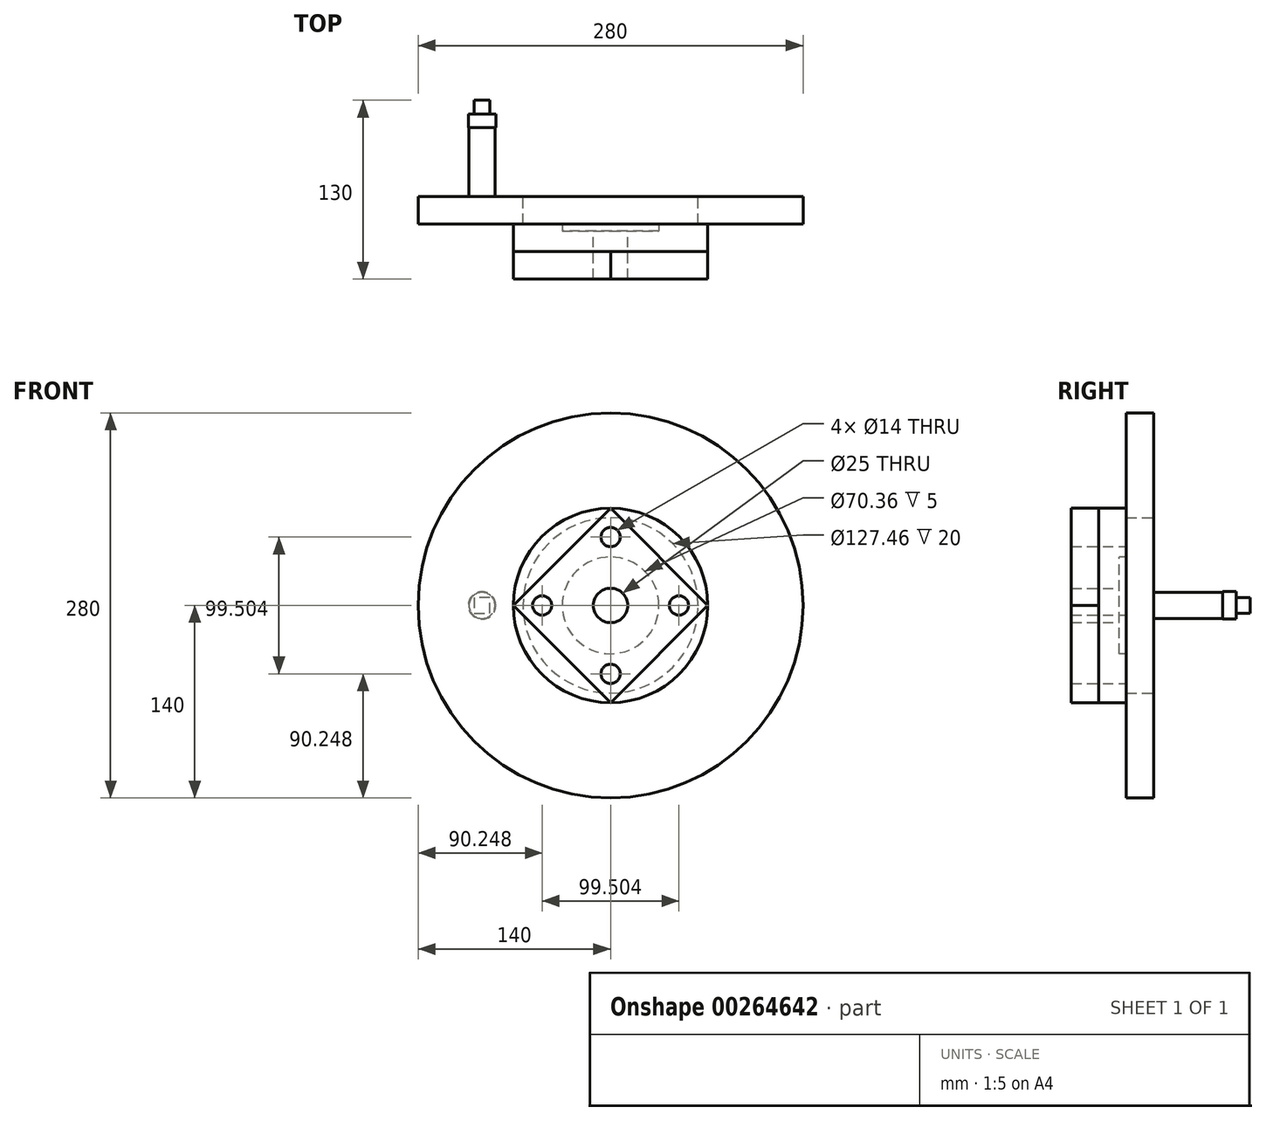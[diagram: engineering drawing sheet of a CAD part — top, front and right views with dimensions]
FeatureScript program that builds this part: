
annotation { "Feature Type Name" : "Feature", "Feature Type Description" : "" }
export const myFeature = defineFeature(function(context is Context, id is Id, definition is map)
    precondition{}
    {
        {
            var Q0;
            Q0=qCreatedBy(makeId("Front.planeOp"),FACE);
            var sketch = newSketch(context, id + "F0", { "sketchPlane" : qUnion([Q0])});
            skLineSegment(sketch, "E0", {"start": v(70.71, 0) * mm, "end": v(0, 70.71) * mm});
            skLineSegment(sketch, "E1", {"start": v(0, 70.71) * mm, "end": v(-70.71, 0) * mm});
            skLineSegment(sketch, "E2", {"start": v(-70.71, 0) * mm, "end": v(0, -70.71) * mm});
            skLineSegment(sketch, "E3", {"start": v(0, -70.71) * mm, "end": v(70.71, 0) * mm});
            skLineSegment(sketch, "E4", {"start": v(0, -49.75) * mm, "end": v(-49.75, 0) * mm, "construction": true});
            skLineSegment(sketch, "E5", {"start": v(-49.75, 0) * mm, "end": v(0, 49.75) * mm, "construction": true});
            skLineSegment(sketch, "E6", {"start": v(0, 49.75) * mm, "end": v(49.75, 0) * mm, "construction": true});
            skLineSegment(sketch, "E7", {"start": v(49.75, 0) * mm, "end": v(0, -49.75) * mm, "construction": true});
            skCircle(sketch, "E8", {"center": v(49.75, 0) * mm, "radius": 7 * mm});
            skCircle(sketch, "E9", {"center": v(0, 49.75) * mm, "radius": 7 * mm});
            skCircle(sketch, "E10", {"center": v(-49.75, 0) * mm, "radius": 7 * mm});
            skCircle(sketch, "E11", {"center": v(0, -49.75) * mm, "radius": 7 * mm});
            skCircle(sketch, "E12", {"center": v(0, 0) * mm, "radius": 35.18 * mm});
            skCircle(sketch, "E13", {"center": v(0, 0) * mm, "radius": 42.75 * mm});
            skCircle(sketch, "E14", {"center": v(0, 0) * mm, "radius": 70.71 * mm});
            skCircle(sketch, "E15", {"center": v(0, 0) * mm, "radius": 12.5 * mm});
            skCircle(sketch, "E16", {"center": v(-93.5, 0) * mm, "radius": 9.5 * mm});
            skCircle(sketch, "E17", {"center": v(0, 0) * mm, "radius": 56.75 * mm});
            skCircle(sketch, "E18", {"center": v(0, 0) * mm, "radius": 63.73 * mm});
            skLineSegment(sketch, "E19", {"start": v(0, 70.71) * mm, "end": v(0, 63.73) * mm, "construction": true});
            skLineSegment(sketch, "E20", {"start": v(0, 63.73) * mm, "end": v(0, 56.75) * mm, "construction": true});
            skCircle(sketch, "E21", {"center": v(0, 0) * mm, "radius": 140 * mm});
            skSolve(sketch);
        }
        {
            var Q0;
            {var subQ1=sQuery(id+"F0.wireOp",EDGE,"E0");var subQ3=sQuery(id+"F0.wireOp",EDGE,"E18");var subQ4=makeQuery(id+"F0.imprint","INTERSECT",VERTEX,{"disambiguationData":[OD(0.0)],"derivedFrom":[subQ1,subQ3]});Q0=makeQuery(id+"F0.imprint","IMPRINT",FACE,{"disambiguationData":[TD([[makeQuery(id+"F0.imprint","IMPRINT",EDGE,{"disambiguationData":[TD([[subQ4,1.0]])],"derivedFrom":subQ3}),-1.0]])]});}
            var Q1;
            {var subQ4=sQuery(id+"F0.wireOp",EDGE,"E0");var subQ6=sQuery(id+"F0.wireOp",EDGE,"E18");var subQ8=makeQuery(id+"F0.imprint","INTERSECT",VERTEX,{"disambiguationData":[OD(0.0)],"derivedFrom":[subQ4,subQ6]});Q1=makeQuery(id+"F0.imprint","IMPRINT",FACE,{"disambiguationData":[TD([[makeQuery(id+"F0.imprint","IMPRINT",EDGE,{"disambiguationData":[TD([[subQ8,-1.0]])],"derivedFrom":subQ4}),1.0]])]});}
            var Q2;
            {var subQ5=sQuery(id+"F0.wireOp",EDGE,"E17");var subQ8=sQuery(id+"F0.wireOp",EDGE,"E0");var subQ9=makeQuery(id+"F0.imprint","INTERSECT",VERTEX,{"disambiguationData":[OD(0.0)],"derivedFrom":[subQ8,subQ5]});Q2=makeQuery(id+"F0.imprint","IMPRINT",FACE,{"disambiguationData":[TD([[makeQuery(id+"F0.imprint","IMPRINT",EDGE,{"disambiguationData":[TD([[subQ9,-1.0]])],"derivedFrom":subQ8}),1.0]])]});}
            var Q3;
            {var subQ0=sQuery(id+"F0.wireOp",EDGE,"E17");var subQ4=sQuery(id+"F0.wireOp",EDGE,"E0");var subQ5=makeQuery(id+"F0.imprint","INTERSECT",VERTEX,{"disambiguationData":[OD(1.0)],"derivedFrom":[subQ4,subQ0]});Q3=makeQuery(id+"F0.imprint","IMPRINT",FACE,{"disambiguationData":[TD([[makeQuery(id+"F0.imprint","IMPRINT",EDGE,{"disambiguationData":[TD([[subQ5,-1.0]])],"derivedFrom":subQ4}),1.0]])]});}
            var Q4;
            {var subQ1=sQuery(id+"F0.wireOp",EDGE,"E0");var subQ3=sQuery(id+"F0.wireOp",EDGE,"E18");var subQ4=makeQuery(id+"F0.imprint","INTERSECT",VERTEX,{"disambiguationData":[OD(1.0)],"derivedFrom":[subQ1,subQ3]});Q4=makeQuery(id+"F0.imprint","IMPRINT",FACE,{"disambiguationData":[TD([[makeQuery(id+"F0.imprint","IMPRINT",EDGE,{"disambiguationData":[TD([[subQ4,-1.0]])],"derivedFrom":subQ3}),-1.0]])]});}
            var Q5;
            {var subQ5=sQuery(id+"F0.wireOp",EDGE,"E17");var subQ8=sQuery(id+"F0.wireOp",EDGE,"E1");var subQ10=makeQuery(id+"F0.imprint","INTERSECT",VERTEX,{"disambiguationData":[OD(0.0)],"derivedFrom":[subQ8,subQ5]});Q5=makeQuery(id+"F0.imprint","IMPRINT",FACE,{"disambiguationData":[TD([[makeQuery(id+"F0.imprint","IMPRINT",EDGE,{"disambiguationData":[TD([[subQ10,-1.0]])],"derivedFrom":subQ8}),1.0]])]});}
            var Q6;
            Q6=makeQuery(id+"F0.imprint","IMPRINT",FACE,{"disambiguationData":[TD([[makeQuery(id+"F0.imprint","IMPRINT",EDGE,{"derivedFrom":sQuery(id+"F0.wireOp",EDGE,"E12")}),-1.0]])]});
            var Q7;
            {var subQ3=sQuery(id+"F0.wireOp",EDGE,"E17");var subQ8=sQuery(id+"F0.wireOp",EDGE,"E3");var subQ9=makeQuery(id+"F0.imprint","INTERSECT",VERTEX,{"disambiguationData":[OD(0.0)],"derivedFrom":[subQ8,subQ3]});Q7=makeQuery(id+"F0.imprint","IMPRINT",FACE,{"disambiguationData":[TD([[makeQuery(id+"F0.imprint","IMPRINT",EDGE,{"disambiguationData":[TD([[subQ9,-1.0]])],"derivedFrom":subQ8}),1.0]])]});}
            var Q8;
            {var subQ5=sQuery(id+"F0.wireOp",EDGE,"E17");var subQ8=sQuery(id+"F0.wireOp",EDGE,"E2");var subQ10=makeQuery(id+"F0.imprint","INTERSECT",VERTEX,{"disambiguationData":[OD(0.0)],"derivedFrom":[subQ8,subQ5]});Q8=makeQuery(id+"F0.imprint","IMPRINT",FACE,{"disambiguationData":[TD([[makeQuery(id+"F0.imprint","IMPRINT",EDGE,{"disambiguationData":[TD([[subQ10,-1.0]])],"derivedFrom":subQ8}),1.0]])]});}
            var Q9;
            {var subQ0=sQuery(id+"F0.wireOp",EDGE,"E17");var subQ1=sQuery(id+"F0.wireOp",EDGE,"E2");var subQ2=makeQuery(id+"F0.imprint","INTERSECT",VERTEX,{"disambiguationData":[OD(1.0)],"derivedFrom":[subQ1,subQ0]});Q9=makeQuery(id+"F0.imprint","IMPRINT",FACE,{"disambiguationData":[TD([[makeQuery(id+"F0.imprint","IMPRINT",EDGE,{"disambiguationData":[TD([[subQ2,-1.0]])],"derivedFrom":subQ1}),1.0]])]});}
            var Q10;
            {var subQ1=sQuery(id+"F0.wireOp",EDGE,"E2");var subQ3=sQuery(id+"F0.wireOp",EDGE,"E18");var subQ4=makeQuery(id+"F0.imprint","INTERSECT",VERTEX,{"disambiguationData":[OD(1.0)],"derivedFrom":[subQ1,subQ3]});Q10=makeQuery(id+"F0.imprint","IMPRINT",FACE,{"disambiguationData":[TD([[makeQuery(id+"F0.imprint","IMPRINT",EDGE,{"disambiguationData":[TD([[subQ4,-1.0]])],"derivedFrom":subQ3}),-1.0]])]});}
            var Q11;
            {var subQ0=sQuery(id+"F0.wireOp",EDGE,"E17");var subQ4=sQuery(id+"F0.wireOp",EDGE,"E1");var subQ5=makeQuery(id+"F0.imprint","INTERSECT",VERTEX,{"disambiguationData":[OD(1.0)],"derivedFrom":[subQ4,subQ0]});Q11=makeQuery(id+"F0.imprint","IMPRINT",FACE,{"disambiguationData":[TD([[makeQuery(id+"F0.imprint","IMPRINT",EDGE,{"disambiguationData":[TD([[subQ5,-1.0]])],"derivedFrom":subQ4}),1.0]])]});}
            var Q12;
            {var subQ1=sQuery(id+"F0.wireOp",EDGE,"E1");var subQ3=sQuery(id+"F0.wireOp",EDGE,"E18");var subQ4=makeQuery(id+"F0.imprint","INTERSECT",VERTEX,{"disambiguationData":[OD(1.0)],"derivedFrom":[subQ1,subQ3]});Q12=makeQuery(id+"F0.imprint","IMPRINT",FACE,{"disambiguationData":[TD([[makeQuery(id+"F0.imprint","IMPRINT",EDGE,{"disambiguationData":[TD([[subQ4,-1.0]])],"derivedFrom":subQ3}),-1.0]])]});}
            var Q13;
            Q13=makeQuery(id+"F0.imprint","IMPRINT",FACE,{"disambiguationData":[TD([[makeQuery(id+"F0.imprint","IMPRINT",EDGE,{"derivedFrom":sQuery(id+"F0.wireOp",EDGE,"E12")}),1.0]])]});
            extrude(context, id + "F1", {"entities" : qUnion([Q0, Q1, Q2, Q3, Q4, Q5, Q6, Q7, Q8, Q9, Q10, Q11, Q12, Q13]), "depth" : 20 * mm});
        }
        {
            var Q0;
            Q0=makeQuery(id+"F0.imprint","IMPRINT",FACE,{"disambiguationData":[TD([[makeQuery(id+"F0.imprint","IMPRINT",EDGE,{"derivedFrom":sQuery(id+"F0.wireOp",EDGE,"E12")}),1.0]])]});
            extrude(context, id + "F2", {"entities" : qUnion([Q0]), "operationType" : NewBodyOperationType.ADD, "oppositeDirection" : true, "depth" : 15 * mm});
        }
        {
            var Q0;
            Q0=makeQuery(id+"F0.imprint","IMPRINT",FACE,{"disambiguationData":[TD([[makeQuery(id+"F0.imprint","IMPRINT",EDGE,{"derivedFrom":sQuery(id+"F0.wireOp",EDGE,"E12")}),-1.0]])]});
            var Q1;
            {var subQ3=sQuery(id+"F0.wireOp",EDGE,"E17");var subQ8=sQuery(id+"F0.wireOp",EDGE,"E3");var subQ9=makeQuery(id+"F0.imprint","INTERSECT",VERTEX,{"disambiguationData":[OD(0.0)],"derivedFrom":[subQ8,subQ3]});Q1=makeQuery(id+"F0.imprint","IMPRINT",FACE,{"disambiguationData":[TD([[makeQuery(id+"F0.imprint","IMPRINT",EDGE,{"disambiguationData":[TD([[subQ9,-1.0]])],"derivedFrom":subQ8}),1.0]])]});}
            var Q2;
            {var subQ0=sQuery(id+"F0.wireOp",EDGE,"E17");var subQ1=sQuery(id+"F0.wireOp",EDGE,"E3");var subQ2=makeQuery(id+"F0.imprint","INTERSECT",VERTEX,{"disambiguationData":[OD(0.0)],"derivedFrom":[subQ1,subQ0]});Q2=makeQuery(id+"F0.imprint","IMPRINT",FACE,{"disambiguationData":[TD([[makeQuery(id+"F0.imprint","IMPRINT",EDGE,{"disambiguationData":[TD([[subQ2,-1.0]])],"derivedFrom":subQ1}),-1.0]])]});}
            var Q3;
            {var subQ0=sQuery(id+"F0.wireOp",EDGE,"E18");var subQ1=sQuery(id+"F0.wireOp",EDGE,"E3");var subQ2=makeQuery(id+"F0.imprint","INTERSECT",VERTEX,{"disambiguationData":[OD(0.0)],"derivedFrom":[subQ1,subQ0]});Q3=makeQuery(id+"F0.imprint","IMPRINT",FACE,{"disambiguationData":[TD([[makeQuery(id+"F0.imprint","IMPRINT",EDGE,{"disambiguationData":[TD([[subQ2,-1.0]])],"derivedFrom":subQ1}),-1.0]])]});}
            var Q4;
            {var subQ1=sQuery(id+"F0.wireOp",EDGE,"E3");var subQ3=sQuery(id+"F0.wireOp",EDGE,"E18");var subQ4=makeQuery(id+"F0.imprint","INTERSECT",VERTEX,{"disambiguationData":[OD(0.0)],"derivedFrom":[subQ1,subQ3]});Q4=makeQuery(id+"F0.imprint","IMPRINT",FACE,{"disambiguationData":[TD([[makeQuery(id+"F0.imprint","IMPRINT",EDGE,{"disambiguationData":[TD([[subQ4,-1.0]])],"derivedFrom":subQ3}),-1.0]])]});}
            var Q5;
            {var subQ4=sQuery(id+"F0.wireOp",EDGE,"E0");var subQ6=sQuery(id+"F0.wireOp",EDGE,"E18");var subQ8=makeQuery(id+"F0.imprint","INTERSECT",VERTEX,{"disambiguationData":[OD(0.0)],"derivedFrom":[subQ4,subQ6]});Q5=makeQuery(id+"F0.imprint","IMPRINT",FACE,{"disambiguationData":[TD([[makeQuery(id+"F0.imprint","IMPRINT",EDGE,{"disambiguationData":[TD([[subQ8,-1.0]])],"derivedFrom":subQ4}),1.0]])]});}
            var Q6;
            {var subQ1=sQuery(id+"F0.wireOp",EDGE,"E0");var subQ3=sQuery(id+"F0.wireOp",EDGE,"E18");var subQ4=makeQuery(id+"F0.imprint","INTERSECT",VERTEX,{"disambiguationData":[OD(0.0)],"derivedFrom":[subQ1,subQ3]});Q6=makeQuery(id+"F0.imprint","IMPRINT",FACE,{"disambiguationData":[TD([[makeQuery(id+"F0.imprint","IMPRINT",EDGE,{"disambiguationData":[TD([[subQ4,1.0]])],"derivedFrom":subQ3}),-1.0]])]});}
            var Q7;
            {var subQ1=sQuery(id+"F0.wireOp",EDGE,"E0");var subQ3=sQuery(id+"F0.wireOp",EDGE,"E18");var subQ4=makeQuery(id+"F0.imprint","INTERSECT",VERTEX,{"disambiguationData":[OD(0.0)],"derivedFrom":[subQ1,subQ3]});Q7=makeQuery(id+"F0.imprint","IMPRINT",FACE,{"disambiguationData":[TD([[makeQuery(id+"F0.imprint","IMPRINT",EDGE,{"disambiguationData":[TD([[subQ4,-1.0]])],"derivedFrom":subQ3}),-1.0]])]});}
            var Q8;
            {var subQ0=sQuery(id+"F0.wireOp",EDGE,"E18");var subQ1=sQuery(id+"F0.wireOp",EDGE,"E0");var subQ2=makeQuery(id+"F0.imprint","INTERSECT",VERTEX,{"disambiguationData":[OD(0.0)],"derivedFrom":[subQ1,subQ0]});Q8=makeQuery(id+"F0.imprint","IMPRINT",FACE,{"disambiguationData":[TD([[makeQuery(id+"F0.imprint","IMPRINT",EDGE,{"disambiguationData":[TD([[subQ2,-1.0]])],"derivedFrom":subQ1}),-1.0]])]});}
            var Q9;
            {var subQ0=sQuery(id+"F0.wireOp",EDGE,"E17");var subQ1=sQuery(id+"F0.wireOp",EDGE,"E0");var subQ2=makeQuery(id+"F0.imprint","INTERSECT",VERTEX,{"disambiguationData":[OD(0.0)],"derivedFrom":[subQ1,subQ0]});Q9=makeQuery(id+"F0.imprint","IMPRINT",FACE,{"disambiguationData":[TD([[makeQuery(id+"F0.imprint","IMPRINT",EDGE,{"disambiguationData":[TD([[subQ2,-1.0]])],"derivedFrom":subQ1}),-1.0]])]});}
            var Q10;
            {var subQ5=sQuery(id+"F0.wireOp",EDGE,"E17");var subQ8=sQuery(id+"F0.wireOp",EDGE,"E0");var subQ9=makeQuery(id+"F0.imprint","INTERSECT",VERTEX,{"disambiguationData":[OD(0.0)],"derivedFrom":[subQ8,subQ5]});Q10=makeQuery(id+"F0.imprint","IMPRINT",FACE,{"disambiguationData":[TD([[makeQuery(id+"F0.imprint","IMPRINT",EDGE,{"disambiguationData":[TD([[subQ9,-1.0]])],"derivedFrom":subQ8}),1.0]])]});}
            var Q11;
            {var subQ0=sQuery(id+"F0.wireOp",EDGE,"E17");var subQ4=sQuery(id+"F0.wireOp",EDGE,"E0");var subQ5=makeQuery(id+"F0.imprint","INTERSECT",VERTEX,{"disambiguationData":[OD(1.0)],"derivedFrom":[subQ4,subQ0]});Q11=makeQuery(id+"F0.imprint","IMPRINT",FACE,{"disambiguationData":[TD([[makeQuery(id+"F0.imprint","IMPRINT",EDGE,{"disambiguationData":[TD([[subQ5,-1.0]])],"derivedFrom":subQ4}),1.0]])]});}
            var Q12;
            {var subQ1=sQuery(id+"F0.wireOp",EDGE,"E0");var subQ3=sQuery(id+"F0.wireOp",EDGE,"E18");var subQ4=makeQuery(id+"F0.imprint","INTERSECT",VERTEX,{"disambiguationData":[OD(1.0)],"derivedFrom":[subQ1,subQ3]});Q12=makeQuery(id+"F0.imprint","IMPRINT",FACE,{"disambiguationData":[TD([[makeQuery(id+"F0.imprint","IMPRINT",EDGE,{"disambiguationData":[TD([[subQ4,-1.0]])],"derivedFrom":subQ3}),-1.0]])]});}
            var Q13;
            {var subQ0=sQuery(id+"F0.wireOp",EDGE,"E18");var subQ1=sQuery(id+"F0.wireOp",EDGE,"E1");var subQ2=makeQuery(id+"F0.imprint","INTERSECT",VERTEX,{"disambiguationData":[OD(0.0)],"derivedFrom":[subQ1,subQ0]});Q13=makeQuery(id+"F0.imprint","IMPRINT",FACE,{"disambiguationData":[TD([[makeQuery(id+"F0.imprint","IMPRINT",EDGE,{"disambiguationData":[TD([[subQ2,-1.0]])],"derivedFrom":subQ1}),-1.0]])]});}
            var Q14;
            {var subQ0=sQuery(id+"F0.wireOp",EDGE,"E17");var subQ1=sQuery(id+"F0.wireOp",EDGE,"E1");var subQ2=makeQuery(id+"F0.imprint","INTERSECT",VERTEX,{"disambiguationData":[OD(0.0)],"derivedFrom":[subQ1,subQ0]});Q14=makeQuery(id+"F0.imprint","IMPRINT",FACE,{"disambiguationData":[TD([[makeQuery(id+"F0.imprint","IMPRINT",EDGE,{"disambiguationData":[TD([[subQ2,-1.0]])],"derivedFrom":subQ1}),-1.0]])]});}
            var Q15;
            {var subQ5=sQuery(id+"F0.wireOp",EDGE,"E17");var subQ8=sQuery(id+"F0.wireOp",EDGE,"E1");var subQ10=makeQuery(id+"F0.imprint","INTERSECT",VERTEX,{"disambiguationData":[OD(0.0)],"derivedFrom":[subQ8,subQ5]});Q15=makeQuery(id+"F0.imprint","IMPRINT",FACE,{"disambiguationData":[TD([[makeQuery(id+"F0.imprint","IMPRINT",EDGE,{"disambiguationData":[TD([[subQ10,-1.0]])],"derivedFrom":subQ8}),1.0]])]});}
            var Q16;
            {var subQ1=sQuery(id+"F0.wireOp",EDGE,"E1");var subQ3=sQuery(id+"F0.wireOp",EDGE,"E18");var subQ4=makeQuery(id+"F0.imprint","INTERSECT",VERTEX,{"disambiguationData":[OD(0.0)],"derivedFrom":[subQ1,subQ3]});Q16=makeQuery(id+"F0.imprint","IMPRINT",FACE,{"disambiguationData":[TD([[makeQuery(id+"F0.imprint","IMPRINT",EDGE,{"disambiguationData":[TD([[subQ4,-1.0]])],"derivedFrom":subQ3}),-1.0]])]});}
            var Q17;
            {var subQ0=sQuery(id+"F0.wireOp",EDGE,"E17");var subQ4=sQuery(id+"F0.wireOp",EDGE,"E1");var subQ5=makeQuery(id+"F0.imprint","INTERSECT",VERTEX,{"disambiguationData":[OD(1.0)],"derivedFrom":[subQ4,subQ0]});Q17=makeQuery(id+"F0.imprint","IMPRINT",FACE,{"disambiguationData":[TD([[makeQuery(id+"F0.imprint","IMPRINT",EDGE,{"disambiguationData":[TD([[subQ5,-1.0]])],"derivedFrom":subQ4}),1.0]])]});}
            var Q18;
            {var subQ1=sQuery(id+"F0.wireOp",EDGE,"E1");var subQ3=sQuery(id+"F0.wireOp",EDGE,"E18");var subQ4=makeQuery(id+"F0.imprint","INTERSECT",VERTEX,{"disambiguationData":[OD(1.0)],"derivedFrom":[subQ1,subQ3]});Q18=makeQuery(id+"F0.imprint","IMPRINT",FACE,{"disambiguationData":[TD([[makeQuery(id+"F0.imprint","IMPRINT",EDGE,{"disambiguationData":[TD([[subQ4,-1.0]])],"derivedFrom":subQ3}),-1.0]])]});}
            var Q19;
            {var subQ1=sQuery(id+"F0.wireOp",EDGE,"E2");var subQ3=sQuery(id+"F0.wireOp",EDGE,"E18");var subQ4=makeQuery(id+"F0.imprint","INTERSECT",VERTEX,{"disambiguationData":[OD(0.0)],"derivedFrom":[subQ1,subQ3]});Q19=makeQuery(id+"F0.imprint","IMPRINT",FACE,{"disambiguationData":[TD([[makeQuery(id+"F0.imprint","IMPRINT",EDGE,{"disambiguationData":[TD([[subQ4,-1.0]])],"derivedFrom":subQ3}),-1.0]])]});}
            var Q20;
            {var subQ0=sQuery(id+"F0.wireOp",EDGE,"E18");var subQ1=sQuery(id+"F0.wireOp",EDGE,"E2");var subQ2=makeQuery(id+"F0.imprint","INTERSECT",VERTEX,{"disambiguationData":[OD(0.0)],"derivedFrom":[subQ1,subQ0]});Q20=makeQuery(id+"F0.imprint","IMPRINT",FACE,{"disambiguationData":[TD([[makeQuery(id+"F0.imprint","IMPRINT",EDGE,{"disambiguationData":[TD([[subQ2,-1.0]])],"derivedFrom":subQ1}),-1.0]])]});}
            var Q21;
            {var subQ0=sQuery(id+"F0.wireOp",EDGE,"E17");var subQ1=sQuery(id+"F0.wireOp",EDGE,"E2");var subQ2=makeQuery(id+"F0.imprint","INTERSECT",VERTEX,{"disambiguationData":[OD(0.0)],"derivedFrom":[subQ1,subQ0]});Q21=makeQuery(id+"F0.imprint","IMPRINT",FACE,{"disambiguationData":[TD([[makeQuery(id+"F0.imprint","IMPRINT",EDGE,{"disambiguationData":[TD([[subQ2,-1.0]])],"derivedFrom":subQ1}),-1.0]])]});}
            var Q22;
            {var subQ5=sQuery(id+"F0.wireOp",EDGE,"E17");var subQ8=sQuery(id+"F0.wireOp",EDGE,"E2");var subQ10=makeQuery(id+"F0.imprint","INTERSECT",VERTEX,{"disambiguationData":[OD(0.0)],"derivedFrom":[subQ8,subQ5]});Q22=makeQuery(id+"F0.imprint","IMPRINT",FACE,{"disambiguationData":[TD([[makeQuery(id+"F0.imprint","IMPRINT",EDGE,{"disambiguationData":[TD([[subQ10,-1.0]])],"derivedFrom":subQ8}),1.0]])]});}
            var Q23;
            {var subQ0=sQuery(id+"F0.wireOp",EDGE,"E17");var subQ1=sQuery(id+"F0.wireOp",EDGE,"E2");var subQ2=makeQuery(id+"F0.imprint","INTERSECT",VERTEX,{"disambiguationData":[OD(1.0)],"derivedFrom":[subQ1,subQ0]});Q23=makeQuery(id+"F0.imprint","IMPRINT",FACE,{"disambiguationData":[TD([[makeQuery(id+"F0.imprint","IMPRINT",EDGE,{"disambiguationData":[TD([[subQ2,-1.0]])],"derivedFrom":subQ1}),1.0]])]});}
            var Q24;
            {var subQ1=sQuery(id+"F0.wireOp",EDGE,"E2");var subQ3=sQuery(id+"F0.wireOp",EDGE,"E18");var subQ4=makeQuery(id+"F0.imprint","INTERSECT",VERTEX,{"disambiguationData":[OD(1.0)],"derivedFrom":[subQ1,subQ3]});Q24=makeQuery(id+"F0.imprint","IMPRINT",FACE,{"disambiguationData":[TD([[makeQuery(id+"F0.imprint","IMPRINT",EDGE,{"disambiguationData":[TD([[subQ4,-1.0]])],"derivedFrom":subQ3}),-1.0]])]});}
            extrude(context, id + "F3", {"entities" : qUnion([Q0, Q1, Q2, Q3, Q4, Q5, Q6, Q7, Q8, Q9, Q10, Q11, Q12, Q13, Q14, Q15, Q16, Q17, Q18, Q19, Q20, Q21, Q22, Q23, Q24]), "operationType" : NewBodyOperationType.ADD, "oppositeDirection" : true, "depth" : 20 * mm});
        }
        {
            var Q0;
            Q0=qCreatedBy(makeId("Top.planeOp"),FACE);
            var sketch = newSketch(context, id + "F4", { "sketchPlane" : qUnion([Q0])});
            skLineSegment(sketch, "E22", {"start": v(-70.71, 0) * mm, "end": v(-63.73, 0) * mm, "construction": true});
            skLineSegment(sketch, "E23", {"start": v(-70.71, 20) * mm, "end": v(-84, 20) * mm});
            skLineSegment(sketch, "E24", {"start": v(-140, 20) * mm, "end": v(-140, 40) * mm});
            skLineSegment(sketch, "E25", {"start": v(-140, 40) * mm, "end": v(-63.73, 40) * mm});
            skLineSegment(sketch, "E26", {"start": v(-63.73, 40) * mm, "end": v(-63.73, 20) * mm});
            skLineSegment(sketch, "E27", {"start": v(-63.73, 20) * mm, "end": v(-70.71, 20) * mm});
            skLineSegment(sketch, "E28", {"start": v(-84, 20) * mm, "end": v(-103, 20) * mm});
            skLineSegment(sketch, "E29", {"start": v(-103, 20) * mm, "end": v(-140, 20) * mm});
            skSolve(sketch);
        }
        {
            var Q0;
            Q0=makeQuery(id+"F4.imprint","IMPRINT",FACE,{"disambiguationData":[TD([[makeQuery(id+"F4.imprint","IMPRINT",EDGE,{"derivedFrom":sQuery(id+"F4.wireOp",EDGE,"E23")}),-1.0]])]});
            var Q1;
            {var subQ0=sQuery(id+"F0.wireOp",EDGE,"E15");Q1=makeQuery(id+"F2.boolean.opBoolean","MERGE",FACE,{"derivedFrom":[makeQuery(id+"F1.opExtrude","SWEPT_FACE",FACE,{"disambiguationData":[OSD([subQ0])]}),makeQuery(id+"F2.opExtrude","SWEPT_FACE",FACE,{"disambiguationData":[OSD([subQ0])]})]});}
            revolve(context, id + "F5", {"operationType" : NewBodyOperationType.ADD, "entities" : qUnion([Q0]), "axis" : qUnion([Q1]), "revolveType" : RevolveType.FULL});
        }
        {
            var Q0;
            Q0=makeQuery(id+"F0.imprint","IMPRINT",FACE,{"disambiguationData":[TD([[makeQuery(id+"F0.imprint","IMPRINT",EDGE,{"derivedFrom":sQuery(id+"F0.wireOp",EDGE,"E16")}),1.0]])]});
            extrude(context, id + "F6", {"entities" : qUnion([Q0]), "operationType" : NewBodyOperationType.REMOVE, "oppositeDirection" : true, "depth" : 92 * mm});
        }
        {
            var Q0;
            Q0=makeQuery(id+"F5.opRevolve","SWEPT_FACE",FACE,{"disambiguationData":[OSD([sQuery(id+"F4.wireOp",EDGE,"E23"),sQuery(id+"F4.wireOp",EDGE,"E27"),sQuery(id+"F4.wireOp",EDGE,"E28"),sQuery(id+"F4.wireOp",EDGE,"E29")])]});
            var sketch = newSketch(context, id + "F7", { "sketchPlane" : qUnion([Q0])});
            skCircle(sketch, "E30.0", {"center": v(-93.5, 0) * mm, "radius": 9.5 * mm});
            skSolve(sketch);
        }
        {
            var Q0;
            Q0 = qSketchRegion(id + "F7", true);
            extrude(context, id + "F8", {"entities" : qUnion([Q0]), "operationType" : NewBodyOperationType.ADD, "oppositeDirection" : true, "depth" : 70 * mm});
        }
        {
            var Q0;
            Q0=makeQuery(id+"F8.opExtrude","CAP_FACE",FACE,{"disambiguationData":[OSD([sQuery(id+"F7.wireOp",EDGE,"E30.0")])],"isStart":false});
            var sketch = newSketch(context, id + "F9", { "sketchPlane" : qUnion([Q0])});
            skCircle(sketch, "E31.0.0", {"center": v(93.5, 0) * mm, "radius": 9.5 * mm, "construction": true});
            skCircle(sketch, "E32", {"center": v(93.5, 0) * mm, "radius": 10 * mm});
            skCircle(sketch, "E33.cCircle", {"center": v(93.5, 0) * mm, "radius": 8 * mm, "construction": true});
            skLineSegment(sketch, "E33.0", {"start": v(87.84, 5.66) * mm, "end": v(99.16, 5.66) * mm});
            skLineSegment(sketch, "E33.1", {"start": v(99.16, 5.66) * mm, "end": v(99.16, -5.66) * mm});
            skLineSegment(sketch, "E33.2", {"start": v(99.16, -5.66) * mm, "end": v(87.84, -5.66) * mm});
            skLineSegment(sketch, "E33.3", {"start": v(87.84, -5.66) * mm, "end": v(87.84, 5.66) * mm});
            skSolve(sketch);
        }
        {
            var Q0;
            Q0=makeQuery(id+"F9.imprint","IMPRINT",FACE,{"disambiguationData":[TD([[makeQuery(id+"F9.imprint","IMPRINT",EDGE,{"derivedFrom":sQuery(id+"F9.wireOp",EDGE,"E33.0")}),-1.0]])]});
            extrude(context, id + "F10", {"entities" : qUnion([Q0]), "operationType" : NewBodyOperationType.ADD, "depth" : 20 * mm});
        }
        {
            var Q0;
            Q0 = qSketchRegion(id + "F9", true);
            extrude(context, id + "F11", {"entities" : qUnion([Q0]), "operationType" : NewBodyOperationType.ADD, "depth" : 10 * mm});
        }
    });
